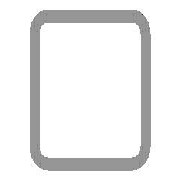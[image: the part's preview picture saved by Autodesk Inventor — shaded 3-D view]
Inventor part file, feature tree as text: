
AUTODESK INVENTOR PART (.ipt)
format: ipt  version: 2025.3 (Build 293356030, 356C)  size: 142,336 bytes
history: native  units: mm (DEFAULTED — no unit token found)
features: other x4, sketch x1, plane x1
ambient origin geometry x8: Origin, YZ Plane, XZ Plane, XY Plane, X Axis, Y Axis, Z Axis, Center Point
bodies: Solid1 (feature_tree), Body (feature_tree)
feature tree (6):
  parser-record x1  (decoder bookkeeping rows leaked as tree rows — omitted from the tree; the rows remain in map.json)
  other  "Driven Length"
  other  "Start Plane"
  other  "End Plane"
  sketch  "Sketch3"  dims[d3=1005.0mm d4=0.0mm d7=6.0mm d9=60.0mm d11=60.0mm d12=3.0mm d13=-0.0mm d14=1005.0mm d15=30.0mm d16=30.0mm d17=90.0deg d18=1005.0mm]
  plane  "Work Plane3"
